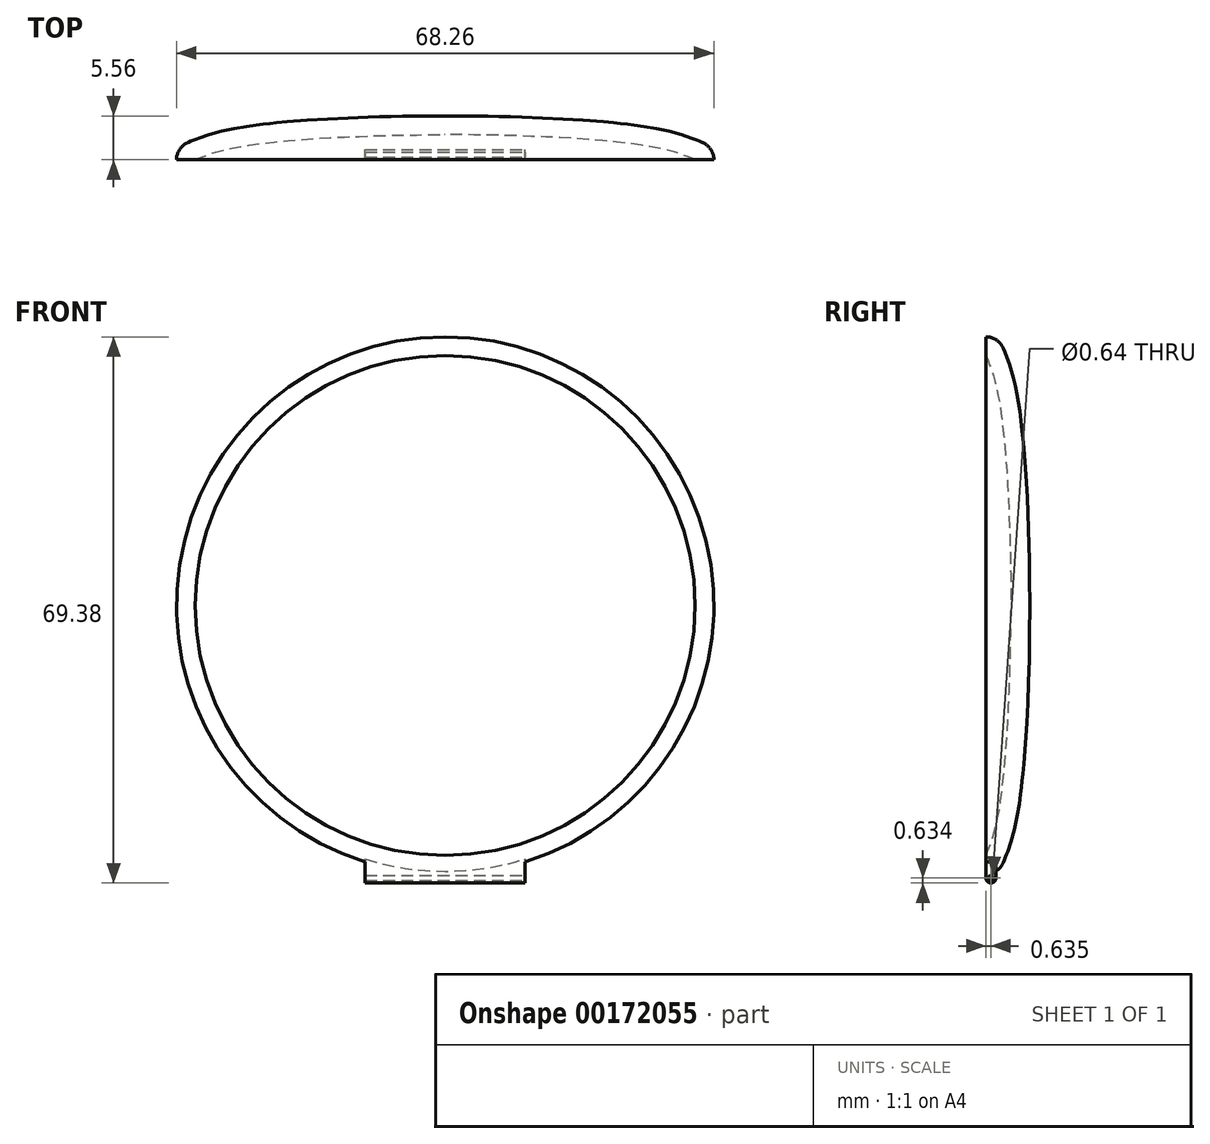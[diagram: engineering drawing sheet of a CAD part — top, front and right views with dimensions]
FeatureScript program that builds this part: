
annotation { "Feature Type Name" : "Feature", "Feature Type Description" : "" }
export const myFeature = defineFeature(function(context is Context, id is Id, definition is map)
    precondition{}
    {
        {
            var Q0;
            Q0=qCreatedBy(makeId("Right.planeOp"),FACE);
            var sketch = newSketch(context, id + "F0", { "sketchPlane" : qUnion([Q0])});
            skPoint(sketch, "E0", {"position": v(3.18, 0) * mm});
            skPoint(sketch, "E1", {"position": v(0, 31.75) * mm});
            skPoint(sketch, "E2", {"position": v(1.59, 26.5) * mm});
            skFitSpline(sketch, "E3", {"points": [v(0, 31.75) * mm, v(1.59, 26.5) * mm, v(3.18, 0) * mm], "startDerivative": vector(5.51, -13.4) * mm, "endDerivative": vector(0, -46.04) * mm});
            skFitSpline(sketch, "E4.0", {"points": [v(2.2, 32.66) * mm, v(2.32, 32.37) * mm, v(2.56, 31.79) * mm, v(2.92, 30.81) * mm, v(3.28, 29.7) * mm, v(3.62, 28.44) * mm, v(3.93, 26.98) * mm, v(4.21, 25.29) * mm, v(4.47, 23.39) * mm, v(4.77, 20.6) * mm, v(5.08, 16.67) * mm, v(5.35, 11.42) * mm, v(5.52, 5.8) * mm, v(5.56, 1.93) * mm, v(5.56, 0) * mm]});
            skArc(sketch, "E5", {"start": v(2.2, 32.66) * mm, "mid": v(1.33, 33.73) * mm, "end": v(0, 34.13) * mm});
            skLineSegment(sketch, "E6", {"start": v(0, 34.13) * mm, "end": v(0, 31.75) * mm});
            skLineSegment(sketch, "E7", {"start": v(5.56, 0) * mm, "end": v(3.18, 0) * mm});
            skSolve(sketch);
        }
        {
            var Q0;
            Q0 = qSketchRegion(id + "F0", true);
            var Q1;
            Q1=sQuery(id+"F0.wireOp",EDGE,"E7");
            revolve(context, id + "F1", {"entities" : qUnion([Q0]), "axis" : qUnion([Q1]), "revolveType" : RevolveType.FULL});
        }
        {
            var Q0;
            Q0=makeQuery(id+"F1.opRevolve","SWEPT_FACE",FACE,{"disambiguationData":[OSD([sQuery(id+"F0.wireOp",EDGE,"E6")])]});
            var sketch = newSketch(context, id + "F2", { "sketchPlane" : qUnion([Q0])});
            skLineSegment(sketch, "E8", {"start": v(-10.16, -35.26) * mm, "end": v(10.16, -35.26) * mm});
            skPoint(sketch, "E9.center.orphan", {"position": v(0, 0) * mm});
            skLineSegment(sketch, "E10", {"start": v(0, 0) * mm, "end": v(0, -46.65) * mm, "construction": true});
            skLineSegment(sketch, "E11", {"start": v(10.16, -35.26) * mm, "end": v(10.16, -30.08) * mm});
            skLineSegment(sketch, "E12", {"start": v(-10.16, -35.26) * mm, "end": v(-10.16, -30.08) * mm});
            skArc(sketch, "E13", {"start": v(-10.16, -30.08) * mm, "mid": v(0, -31.75) * mm, "end": v(10.16, -30.08) * mm});
            skSolve(sketch);
        }
        {
            var Q0;
            Q0 = qSketchRegion(id + "F2", true);
            extrude(context, id + "F3", {"entities" : qUnion([Q0]), "operationType" : NewBodyOperationType.ADD, "oppositeDirection" : true, "depth" : 1.27 * mm});
        }
        {
            var Q0;
            Q0=makeQuery(id+"F3.opExtrude","SWEPT_FACE",FACE,{"disambiguationData":[OSD([sQuery(id+"F2.wireOp",EDGE,"E11")])]});
            var sketch = newSketch(context, id + "F4", { "sketchPlane" : qUnion([Q0])});
            skCircle(sketch, "E14", {"center": v(0.64, -34.62) * mm, "radius": 0.32 * mm});
            skArc(sketch, "E15", {"start": v(1.27, -34.62) * mm, "mid": v(0.64, -35.25) * mm, "end": v(0, -34.62) * mm});
            skLineSegment(sketch, "E16", {"start": v(0, -34.62) * mm, "end": v(0, -35.26) * mm});
            skLineSegment(sketch, "E17", {"start": v(0, -35.26) * mm, "end": v(1.27, -35.26) * mm});
            skLineSegment(sketch, "E18", {"start": v(1.27, -35.26) * mm, "end": v(1.27, -34.62) * mm});
            skSolve(sketch);
        }
        {
            var Q0;
            Q0 = qSketchRegion(id + "F4", true);
            extrude(context, id + "F5", {"entities" : qUnion([Q0]), "operationType" : NewBodyOperationType.REMOVE, "endBound" : BoundingType.THROUGH_ALL, "oppositeDirection" : true, "depth" : 25.4 * mm});
        }
    });
